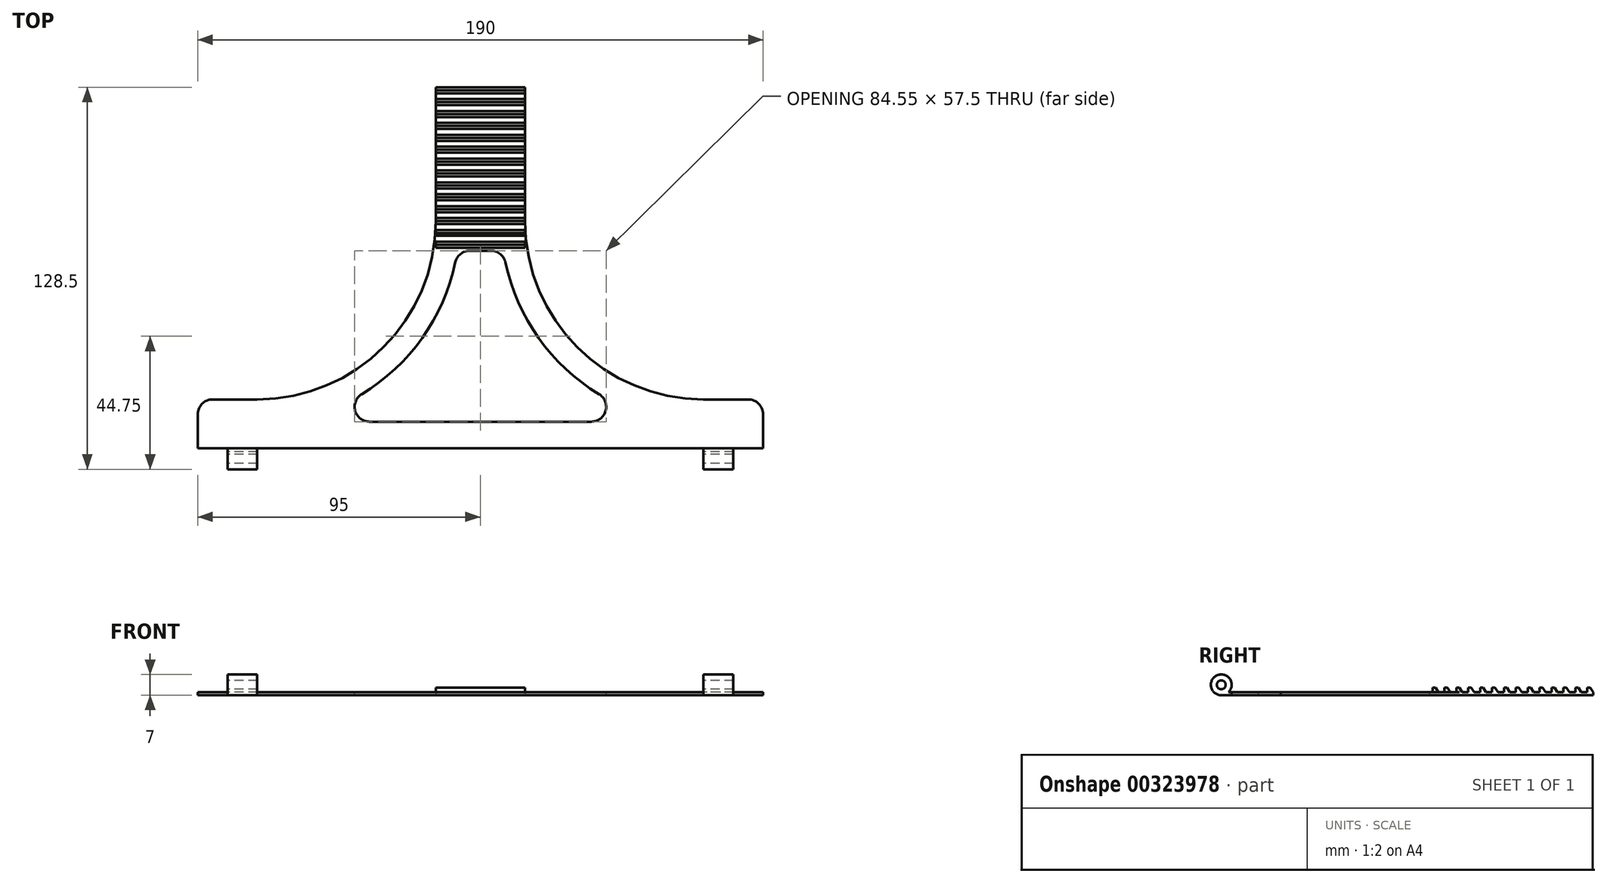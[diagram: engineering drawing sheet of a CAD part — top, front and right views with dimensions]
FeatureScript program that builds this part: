
annotation { "Feature Type Name" : "Feature", "Feature Type Description" : "" }
export const myFeature = defineFeature(function(context is Context, id is Id, definition is map)
    precondition{}
    {
        {
            var Q0;
            Q0=qCreatedBy(makeId("Top.planeOp"),FACE);
            var sketch = newSketch(context, id + "F0", { "sketchPlane" : qUnion([Q0])});
            skLineSegment(sketch, "E0", {"start": v(0, 0) * mm, "end": v(190, 0) * mm});
            skLineSegment(sketch, "E1", {"start": v(190, 0) * mm, "end": v(190, 20) * mm});
            skLineSegment(sketch, "E2", {"start": v(190, 20) * mm, "end": v(110, 20) * mm});
            skLineSegment(sketch, "E3", {"start": v(110, 20) * mm, "end": v(110, 125) * mm});
            skLineSegment(sketch, "E4", {"start": v(110, 125) * mm, "end": v(80, 125) * mm});
            skLineSegment(sketch, "E5", {"start": v(80, 125) * mm, "end": v(80, 20) * mm});
            skLineSegment(sketch, "E6", {"start": v(80, 20) * mm, "end": v(0, 20) * mm});
            skLineSegment(sketch, "E7", {"start": v(0, 20) * mm, "end": v(0, 0) * mm});
            skSolve(sketch);
        }
        {
            var Q0;
            Q0 = qSketchRegion(id + "F0", true);
            extrude(context, id + "F1", {"entities" : qUnion([Q0]), "depth" : 1 * mm});
        }
        {
            var Q0;
            Q0=makeQuery(id+"F1.opExtrude","SWEPT_FACE",FACE,{"disambiguationData":[OSD([sQuery(id+"F0.wireOp",EDGE,"E7")])]});
            var sketch = newSketch(context, id + "F2", { "sketchPlane" : qUnion([Q0])});
            skCircle(sketch, "E8", {"center": v(0, 3.5) * mm, "radius": 1.5 * mm});
            skCircle(sketch, "E9", {"center": v(0, 3.5) * mm, "radius": 3.5 * mm});
            skSolve(sketch);
        }
        {
            var Q0;
            Q0 = qSketchRegion(id + "F2", true);
            var Q1;
            Q1=makeQuery(id+"F1.opExtrude","SWEPT_FACE",FACE,{"disambiguationData":[OSD([sQuery(id+"F0.wireOp",EDGE,"E1")])]});
            extrude(context, id + "F3", {"entities" : qUnion([Q0]), "operationType" : NewBodyOperationType.ADD, "endBound" : BoundingType.UP_TO_SURFACE, "oppositeDirection" : true, "endBoundEntityFace" : qUnion([Q1]), "depth" : 25 * mm});
        }
        {
            var Q0;
            Q0=makeQuery(id+"F1.opExtrude","SWEPT_FACE",FACE,{"disambiguationData":[OSD([sQuery(id+"F0.wireOp",EDGE,"E4")])]});
            var sketch = newSketch(context, id + "F4", { "sketchPlane" : qUnion([Q0])});
            skPoint(sketch, "E10.0", {"position": v(-190, 1) * mm});
            skPoint(sketch, "E11.0", {"position": v(0, 1) * mm});
            skLineSegment(sketch, "E12.bottom", {"start": v(-190, 1) * mm, "end": v(-180, 1) * mm});
            skLineSegment(sketch, "E12.top", {"start": v(-190, 21) * mm, "end": v(-180, 21) * mm});
            skLineSegment(sketch, "E12.left", {"start": v(-190, 1) * mm, "end": v(-190, 21) * mm});
            skLineSegment(sketch, "E12.right", {"start": v(-180, 1) * mm, "end": v(-180, 21) * mm});
            skLineSegment(sketch, "E13.bottom", {"start": v(0, 1) * mm, "end": v(-10, 1) * mm});
            skLineSegment(sketch, "E13.top", {"start": v(0, 21) * mm, "end": v(-10, 21) * mm});
            skLineSegment(sketch, "E13.left", {"start": v(0, 1) * mm, "end": v(0, 21) * mm});
            skLineSegment(sketch, "E13.right", {"start": v(-10, 1) * mm, "end": v(-10, 21) * mm});
            skLineSegment(sketch, "E14.bottom", {"start": v(-170, 21) * mm, "end": v(-20, 21) * mm});
            skLineSegment(sketch, "E14.top", {"start": v(-170, 1) * mm, "end": v(-20, 1) * mm});
            skLineSegment(sketch, "E14.left", {"start": v(-170, 21) * mm, "end": v(-170, 1) * mm});
            skLineSegment(sketch, "E14.right", {"start": v(-20, 21) * mm, "end": v(-20, 1) * mm});
            skSolve(sketch);
        }
        {
            var Q0;
            Q0 = qSketchRegion(id + "F4", true);
            extrude(context, id + "F5", {"entities" : qUnion([Q0]), "operationType" : NewBodyOperationType.REMOVE, "endBound" : BoundingType.THROUGH_ALL, "oppositeDirection" : true, "depth" : 25 * mm});
        }
        {
            var Q0;
            Q0=makeQuery(id+"F5.boolean.opBoolean","MERGE",FACE,{"derivedFrom":[makeQuery(id+"F1.opExtrude","CAP_FACE",FACE,{"disambiguationData":[OSD([sQuery(id+"F0.wireOp",EDGE,"E0"),sQuery(id+"F0.wireOp",EDGE,"E1"),sQuery(id+"F0.wireOp",EDGE,"E2"),sQuery(id+"F0.wireOp",EDGE,"E3"),sQuery(id+"F0.wireOp",EDGE,"E4"),sQuery(id+"F0.wireOp",EDGE,"E5"),sQuery(id+"F0.wireOp",EDGE,"E6"),sQuery(id+"F0.wireOp",EDGE,"E7")])],"isStart":false}),makeQuery(id+"F5.opExtrude","SWEPT_FACE",FACE,{"disambiguationData":[OSD([sQuery(id+"F4.wireOp",EDGE,"E12.bottom")])]}),makeQuery(id+"F5.opExtrude","SWEPT_FACE",FACE,{"disambiguationData":[OSD([sQuery(id+"F4.wireOp",EDGE,"E13.bottom")])]}),makeQuery(id+"F5.opExtrude","SWEPT_FACE",FACE,{"disambiguationData":[OSD([sQuery(id+"F4.wireOp",EDGE,"E14.top")])]})]});
            var sketch = newSketch(context, id + "F6", { "sketchPlane" : qUnion([Q0])});
            skLineSegment(sketch, "E15.bottom", {"start": v(0, -2.45) * mm, "end": v(10, -2.45) * mm});
            skLineSegment(sketch, "E15.top", {"start": v(0, 3.5) * mm, "end": v(10, 3.5) * mm});
            skLineSegment(sketch, "E15.left", {"start": v(0, -2.45) * mm, "end": v(0, 3.5) * mm});
            skLineSegment(sketch, "E15.right", {"start": v(10, -2.45) * mm, "end": v(10, 3.5) * mm});
            skLineSegment(sketch, "E16.bottom", {"start": v(190, -2.45) * mm, "end": v(180, -2.45) * mm});
            skLineSegment(sketch, "E16.top", {"start": v(190, 3.5) * mm, "end": v(180, 3.5) * mm});
            skLineSegment(sketch, "E16.left", {"start": v(190, -2.45) * mm, "end": v(190, 3.5) * mm});
            skLineSegment(sketch, "E16.right", {"start": v(180, -2.45) * mm, "end": v(180, 3.5) * mm});
            skLineSegment(sketch, "E17.0", {"start": v(20, -3.5) * mm, "end": v(20, 3.5) * mm});
            skLineSegment(sketch, "E18.bottom", {"start": v(20, -3.5) * mm, "end": v(170, -3.5) * mm});
            skLineSegment(sketch, "E18.top", {"start": v(20, 3.5) * mm, "end": v(170, 3.5) * mm});
            skLineSegment(sketch, "E18.right", {"start": v(170, -3.5) * mm, "end": v(170, 3.5) * mm});
            skSolve(sketch);
        }
        {
            var Q0;
            Q0 = qSketchRegion(id + "F6", true);
            extrude(context, id + "F7", {"entities" : qUnion([Q0]), "operationType" : NewBodyOperationType.REMOVE, "endBound" : BoundingType.THROUGH_ALL, "oppositeDirection" : true, "depth" : 25 * mm});
        }
        {
            var Q0;
            Q0=makeQuery(id+"F7.boolean.opBoolean","COPY",EDGE,{"derivedFrom":makeQuery(id+"F7.opExtrude","SWEPT_EDGE",EDGE,{"disambiguationData":[OSD([sQuery(id+"F0.wireOp",EDGE,"E7"),sQuery(id+"F4.wireOp",EDGE,"E13.bottom"),sQuery(id+"F4.wireOp",EDGE,"E13.left"),sQuery(id+"F6.wireOp",EDGE,"E15.top"),sQuery(id+"F6.wireOp",EDGE,"E15.left")])]})});
            var Q1;
            Q1=makeQuery(id+"F1.opExtrude","SWEPT_EDGE",EDGE,{"disambiguationData":[OSD([sQuery(id+"F0.wireOp",EDGE,"E6"),sQuery(id+"F0.wireOp",EDGE,"E7")])]});
            var Q2;
            Q2=makeQuery(id+"F7.boolean.opBoolean","COPY",EDGE,{"derivedFrom":makeQuery(id+"F7.opExtrude","SWEPT_EDGE",EDGE,{"disambiguationData":[OSD([sQuery(id+"F0.wireOp",EDGE,"E1"),sQuery(id+"F4.wireOp",EDGE,"E12.bottom"),sQuery(id+"F4.wireOp",EDGE,"E12.left"),sQuery(id+"F6.wireOp",EDGE,"E16.top"),sQuery(id+"F6.wireOp",EDGE,"E16.left")])]})});
            var Q3;
            Q3=makeQuery(id+"F1.opExtrude","SWEPT_EDGE",EDGE,{"disambiguationData":[OSD([sQuery(id+"F0.wireOp",EDGE,"E1"),sQuery(id+"F0.wireOp",EDGE,"E2")])]});
            fillet(context, id + "F8", {"entities" : qUnion([Q0, Q1, Q2, Q3]), "radius" : 5 * mm, "tangentPropagation" : true, "allowEdgeOverflow" : false});
        }
        {
            var Q0;
            Q0=makeQuery(id+"F1.opExtrude","SWEPT_EDGE",EDGE,{"disambiguationData":[OSD([sQuery(id+"F0.wireOp",EDGE,"E5"),sQuery(id+"F0.wireOp",EDGE,"E6")])]});
            var Q1;
            Q1=makeQuery(id+"F1.opExtrude","SWEPT_EDGE",EDGE,{"disambiguationData":[OSD([sQuery(id+"F0.wireOp",EDGE,"E2"),sQuery(id+"F0.wireOp",EDGE,"E3")])]});
            fillet(context, id + "F9", {"entities" : qUnion([Q0, Q1]), "radius" : 60 * mm, "tangentPropagation" : true, "allowEdgeOverflow" : false});
        }
        {
            var Q0;
            Q0=makeQuery(id+"F1.opExtrude","SWEPT_FACE",FACE,{"disambiguationData":[OSD([sQuery(id+"F0.wireOp",EDGE,"E5")])]});
            var sketch = newSketch(context, id + "F10", { "sketchPlane" : qUnion([Q0])});
            skLineSegment(sketch, "E19", {"start": v(-125, 1) * mm, "end": v(-124, 2.5) * mm});
            skLineSegment(sketch, "E20", {"start": v(-124, 2.5) * mm, "end": v(-123, 2.5) * mm});
            skLineSegment(sketch, "E21", {"start": v(-123, 2.5) * mm, "end": v(-123, 1) * mm});
            skLineSegment(sketch, "E22", {"start": v(-123, 1) * mm, "end": v(-121, 1) * mm});
            skLineSegment(sketch, "E23.1.0.0", {"start": v(-120, 2.5) * mm, "end": v(-119, 2.5) * mm});
            skLineSegment(sketch, "E23.1.0.1", {"start": v(-119, 1) * mm, "end": v(-117, 1) * mm});
            skLineSegment(sketch, "E23.1.0.2", {"start": v(-121, 1) * mm, "end": v(-120, 2.5) * mm});
            skLineSegment(sketch, "E23.1.0.3", {"start": v(-119, 2.5) * mm, "end": v(-119, 1) * mm});
            skLineSegment(sketch, "E23.2.0.0", {"start": v(-116, 2.5) * mm, "end": v(-115, 2.5) * mm});
            skLineSegment(sketch, "E23.2.0.1", {"start": v(-115, 1) * mm, "end": v(-113, 1) * mm});
            skLineSegment(sketch, "E23.2.0.2", {"start": v(-117, 1) * mm, "end": v(-116, 2.5) * mm});
            skLineSegment(sketch, "E23.2.0.3", {"start": v(-115, 2.5) * mm, "end": v(-115, 1) * mm});
            skLineSegment(sketch, "E23.3.0.0", {"start": v(-112, 2.5) * mm, "end": v(-111, 2.5) * mm});
            skLineSegment(sketch, "E23.3.0.1", {"start": v(-111, 1) * mm, "end": v(-109, 1) * mm});
            skLineSegment(sketch, "E23.3.0.2", {"start": v(-113, 1) * mm, "end": v(-112, 2.5) * mm});
            skLineSegment(sketch, "E23.3.0.3", {"start": v(-111, 2.5) * mm, "end": v(-111, 1) * mm});
            skLineSegment(sketch, "E23.4.0.0", {"start": v(-108, 2.5) * mm, "end": v(-107, 2.5) * mm});
            skLineSegment(sketch, "E23.4.0.1", {"start": v(-107, 1) * mm, "end": v(-105, 1) * mm});
            skLineSegment(sketch, "E23.4.0.2", {"start": v(-109, 1) * mm, "end": v(-108, 2.5) * mm});
            skLineSegment(sketch, "E23.4.0.3", {"start": v(-107, 2.5) * mm, "end": v(-107, 1) * mm});
            skLineSegment(sketch, "E23.5.0.0", {"start": v(-104, 2.5) * mm, "end": v(-103, 2.5) * mm});
            skLineSegment(sketch, "E23.5.0.1", {"start": v(-103, 1) * mm, "end": v(-101, 1) * mm});
            skLineSegment(sketch, "E23.5.0.2", {"start": v(-105, 1) * mm, "end": v(-104, 2.5) * mm});
            skLineSegment(sketch, "E23.5.0.3", {"start": v(-103, 2.5) * mm, "end": v(-103, 1) * mm});
            skLineSegment(sketch, "E23.6.0.0", {"start": v(-100, 2.5) * mm, "end": v(-99, 2.5) * mm});
            skLineSegment(sketch, "E23.6.0.1", {"start": v(-99, 1) * mm, "end": v(-97, 1) * mm});
            skLineSegment(sketch, "E23.6.0.2", {"start": v(-101, 1) * mm, "end": v(-100, 2.5) * mm});
            skLineSegment(sketch, "E23.6.0.3", {"start": v(-99, 2.5) * mm, "end": v(-99, 1) * mm});
            skLineSegment(sketch, "E23.7.0.0", {"start": v(-96, 2.5) * mm, "end": v(-95, 2.5) * mm});
            skLineSegment(sketch, "E23.7.0.1", {"start": v(-95, 1) * mm, "end": v(-93, 1) * mm});
            skLineSegment(sketch, "E23.7.0.2", {"start": v(-97, 1) * mm, "end": v(-96, 2.5) * mm});
            skLineSegment(sketch, "E23.7.0.3", {"start": v(-95, 2.5) * mm, "end": v(-95, 1) * mm});
            skLineSegment(sketch, "E23.8.0.0", {"start": v(-92, 2.5) * mm, "end": v(-91, 2.5) * mm});
            skLineSegment(sketch, "E23.8.0.1", {"start": v(-91, 1) * mm, "end": v(-89, 1) * mm});
            skLineSegment(sketch, "E23.8.0.2", {"start": v(-93, 1) * mm, "end": v(-92, 2.5) * mm});
            skLineSegment(sketch, "E23.8.0.3", {"start": v(-91, 2.5) * mm, "end": v(-91, 1) * mm});
            skLineSegment(sketch, "E23.9.0.0", {"start": v(-88, 2.5) * mm, "end": v(-87, 2.5) * mm});
            skLineSegment(sketch, "E23.9.0.1", {"start": v(-87, 1) * mm, "end": v(-85, 1) * mm});
            skLineSegment(sketch, "E23.9.0.2", {"start": v(-89, 1) * mm, "end": v(-88, 2.5) * mm});
            skLineSegment(sketch, "E23.9.0.3", {"start": v(-87, 2.5) * mm, "end": v(-87, 1) * mm});
            skLineSegment(sketch, "E23.10.0.0", {"start": v(-84, 2.5) * mm, "end": v(-83, 2.5) * mm});
            skLineSegment(sketch, "E23.10.0.1", {"start": v(-83, 1) * mm, "end": v(-81, 1) * mm});
            skLineSegment(sketch, "E23.10.0.2", {"start": v(-85, 1) * mm, "end": v(-84, 2.5) * mm});
            skLineSegment(sketch, "E23.10.0.3", {"start": v(-83, 2.5) * mm, "end": v(-83, 1) * mm});
            skLineSegment(sketch, "E23.11.0.0", {"start": v(-80, 2.5) * mm, "end": v(-79, 2.5) * mm});
            skLineSegment(sketch, "E23.11.0.1", {"start": v(-79, 1) * mm, "end": v(-77, 1) * mm});
            skLineSegment(sketch, "E23.11.0.2", {"start": v(-81, 1) * mm, "end": v(-80, 2.5) * mm});
            skLineSegment(sketch, "E23.11.0.3", {"start": v(-79, 2.5) * mm, "end": v(-79, 1) * mm});
            skLineSegment(sketch, "E23.12.0.0", {"start": v(-76, 2.5) * mm, "end": v(-75, 2.5) * mm});
            skLineSegment(sketch, "E23.12.0.1", {"start": v(-75, 1) * mm, "end": v(-73, 1) * mm});
            skLineSegment(sketch, "E23.12.0.2", {"start": v(-77, 1) * mm, "end": v(-76, 2.5) * mm});
            skLineSegment(sketch, "E23.12.0.3", {"start": v(-75, 2.5) * mm, "end": v(-75, 1) * mm});
            skLineSegment(sketch, "E23.13.0.0", {"start": v(-72, 2.5) * mm, "end": v(-71, 2.5) * mm});
            skLineSegment(sketch, "E23.13.0.1", {"start": v(-71, 1) * mm, "end": v(-69, 1) * mm});
            skLineSegment(sketch, "E23.13.0.2", {"start": v(-73, 1) * mm, "end": v(-72, 2.5) * mm});
            skLineSegment(sketch, "E23.13.0.3", {"start": v(-71, 2.5) * mm, "end": v(-71, 1) * mm});
            skLineSegment(sketch, "E23.direction1", {"start": v(-125, 1) * mm, "end": v(-121, 1) * mm, "construction": true});
            skLineSegment(sketch, "E24", {"start": v(-125, 1) * mm, "end": v(-125, 0) * mm});
            skLineSegment(sketch, "E25", {"start": v(-125, 0) * mm, "end": v(-80, 0) * mm});
            skLineSegment(sketch, "E26", {"start": v(-80, 0) * mm, "end": v(-69, 1) * mm});
            skSolve(sketch);
        }
        {
            var Q0;
            Q0 = qSketchRegion(id + "F10", true);
            var Q1;
            Q1=makeQuery(id+"F1.opExtrude","SWEPT_FACE",FACE,{"disambiguationData":[OSD([sQuery(id+"F0.wireOp",EDGE,"E3")])]});
            extrude(context, id + "F11", {"entities" : qUnion([Q0]), "operationType" : NewBodyOperationType.ADD, "endBound" : BoundingType.UP_TO_SURFACE, "oppositeDirection" : true, "endBoundEntityFace" : qUnion([Q1]), "depth" : 25 * mm});
        }
        {
            var Q0;
            {var subQ0=sQuery(id+"F0.wireOp",EDGE,"E2");var subQ1=sQuery(id+"F0.wireOp",EDGE,"E1");var subQ4=sQuery(id+"F0.wireOp",EDGE,"E6");var subQ5=sQuery(id+"F0.wireOp",EDGE,"E5");var subQ6=sQuery(id+"F0.wireOp",EDGE,"E7");var subQ8=sQuery(id+"F4.wireOp",EDGE,"E13.bottom");var subQ9=sQuery(id+"F0.wireOp",EDGE,"E3");var subQ11=sQuery(id+"F4.wireOp",EDGE,"E12.bottom");Q0=makeQuery(id+"F11.boolean.opBoolean","SPLIT",FACE,{"disambiguationData":[TD([makeQuery(id+"F1.opExtrude","SWEPT_FACE",FACE,{"disambiguationData":[OSD([subQ1])]})])],"derivedFrom":makeQuery(id+"F5.boolean.opBoolean","MERGE",FACE,{"derivedFrom":[makeQuery(id+"F1.opExtrude","CAP_FACE",FACE,{"disambiguationData":[OSD([sQuery(id+"F0.wireOp",EDGE,"E0"),subQ1,subQ0,subQ9,sQuery(id+"F0.wireOp",EDGE,"E4"),subQ5,subQ4,subQ6])],"isStart":false}),makeQuery(id+"F5.opExtrude","SWEPT_FACE",FACE,{"disambiguationData":[OSD([subQ11])]}),makeQuery(id+"F5.opExtrude","SWEPT_FACE",FACE,{"disambiguationData":[OSD([subQ8])]}),makeQuery(id+"F5.opExtrude","SWEPT_FACE",FACE,{"disambiguationData":[OSD([sQuery(id+"F4.wireOp",EDGE,"E14.top")])]})]})});}
            var sketch = newSketch(context, id + "F12", { "sketchPlane" : qUnion([Q0])});
            skLineSegment(sketch, "E27.0", {"start": v(102.74, 70) * mm, "end": v(87.26, 70) * mm});
            skArc(sketch, "E28.0", {"start": v(87.26, 70) * mm, "mid": v(67.45, 31.29) * mm, "end": v(28.23, 12.5) * mm});
            skArc(sketch, "E29.0", {"start": v(161.77, 12.5) * mm, "mid": v(122.55, 31.29) * mm, "end": v(102.74, 70) * mm});
            skLineSegment(sketch, "E30.0", {"start": v(28.23, 12.5) * mm, "end": v(161.77, 12.5) * mm});
            skSolve(sketch);
        }
        {
            var Q0;
            Q0 = qSketchRegion(id + "F12", true);
            extrude(context, id + "F13", {"entities" : qUnion([Q0]), "operationType" : NewBodyOperationType.REMOVE, "endBound" : BoundingType.THROUGH_ALL, "oppositeDirection" : true, "depth" : 25 * mm});
        }
        {
            var Q0;
            Q0=makeQuery(id+"F13.boolean.opBoolean","COPY",EDGE,{"derivedFrom":makeQuery(id+"F13.opExtrude","SWEPT_EDGE",EDGE,{"disambiguationData":[OSD([sQuery(id+"F12.wireOp",EDGE,"E28.0"),sQuery(id+"F12.wireOp",EDGE,"E30.0")])]})});
            var Q1;
            Q1=makeQuery(id+"F13.boolean.opBoolean","COPY",EDGE,{"derivedFrom":makeQuery(id+"F13.opExtrude","SWEPT_EDGE",EDGE,{"disambiguationData":[OSD([sQuery(id+"F12.wireOp",EDGE,"E29.0"),sQuery(id+"F12.wireOp",EDGE,"E30.0")])]})});
            var Q2;
            Q2=makeQuery(id+"F13.boolean.opBoolean","COPY",EDGE,{"derivedFrom":makeQuery(id+"F13.opExtrude","SWEPT_EDGE",EDGE,{"disambiguationData":[OSD([sQuery(id+"F12.wireOp",EDGE,"E27.0"),sQuery(id+"F12.wireOp",EDGE,"E28.0")])]})});
            var Q3;
            Q3=makeQuery(id+"F13.boolean.opBoolean","COPY",EDGE,{"derivedFrom":makeQuery(id+"F13.opExtrude","SWEPT_EDGE",EDGE,{"disambiguationData":[OSD([sQuery(id+"F12.wireOp",EDGE,"E27.0"),sQuery(id+"F12.wireOp",EDGE,"E29.0")])]})});
            fillet(context, id + "F14", {"entities" : qUnion([Q0, Q1, Q2, Q3]), "radius" : 5 * mm, "tangentPropagation" : true, "allowEdgeOverflow" : false});
        }
    });
